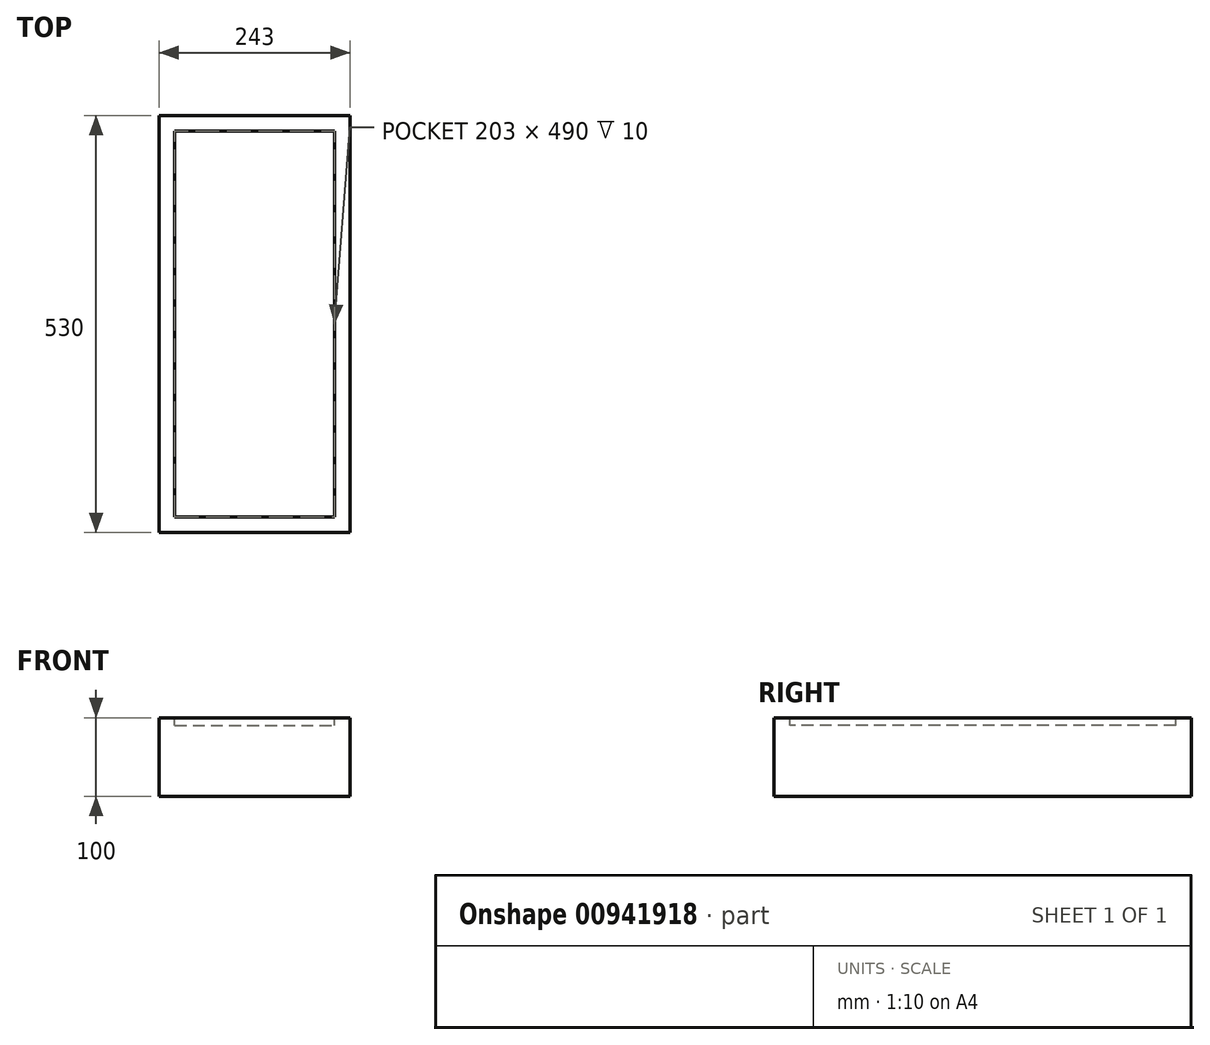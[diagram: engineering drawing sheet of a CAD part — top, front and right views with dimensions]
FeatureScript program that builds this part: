
annotation { "Feature Type Name" : "Feature", "Feature Type Description" : "" }
export const myFeature = defineFeature(function(context is Context, id is Id, definition is map)
    precondition{}
    {
        {
            var Q0;
            Q0=qCreatedBy(makeId("Top.planeOp"),FACE);
            var sketch = newSketch(context, id + "F0", { "sketchPlane" : qUnion([Q0])});
            skLineSegment(sketch, "E0.bottom", {"start": v(-266.27, 176.22) * mm, "end": v(-23.27, 176.22) * mm});
            skLineSegment(sketch, "E0.top", {"start": v(-266.27, -353.78) * mm, "end": v(-23.27, -353.78) * mm});
            skLineSegment(sketch, "E0.left", {"start": v(-266.27, 176.22) * mm, "end": v(-266.27, -353.78) * mm});
            skLineSegment(sketch, "E0.right", {"start": v(-23.27, 176.22) * mm, "end": v(-23.27, -353.78) * mm});
            skLineSegment(sketch, "E1.bottom", {"start": v(-246.27, 156.22) * mm, "end": v(-43.27, 156.22) * mm});
            skLineSegment(sketch, "E1.top", {"start": v(-246.27, -333.78) * mm, "end": v(-43.27, -333.78) * mm});
            skLineSegment(sketch, "E1.left", {"start": v(-246.27, 156.22) * mm, "end": v(-246.27, -333.78) * mm});
            skLineSegment(sketch, "E1.right", {"start": v(-43.27, 156.22) * mm, "end": v(-43.27, -333.78) * mm});
            skSolve(sketch);
        }
        {
            var Q0;
            Q0=makeQuery(id+"F0.imprint","IMPRINT",FACE,{"disambiguationData":[TD([[makeQuery(id+"F0.imprint","IMPRINT",EDGE,{"derivedFrom":sQuery(id+"F0.wireOp",EDGE,"E0.bottom")}),-1.0]])]});
            var Q1;
            Q1=makeQuery(id+"F0.imprint","IMPRINT",FACE,{"disambiguationData":[TD([[makeQuery(id+"F0.imprint","IMPRINT",EDGE,{"derivedFrom":sQuery(id+"F0.wireOp",EDGE,"E1.bottom")}),-1.0]])]});
            extrude(context, id + "F1", {"entities" : qUnion([Q0, Q1]), "oppositeDirection" : true, "depth" : 100 * mm, "offsetDistance" : 25 * mm});
        }
        {
            var Q0;
            Q0=makeQuery(id+"F0.imprint","IMPRINT",FACE,{"disambiguationData":[TD([[makeQuery(id+"F0.imprint","IMPRINT",EDGE,{"derivedFrom":sQuery(id+"F0.wireOp",EDGE,"E1.bottom")}),-1.0]])]});
            extrude(context, id + "F2", {"entities" : qUnion([Q0]), "operationType" : NewBodyOperationType.REMOVE, "oppositeDirection" : true, "depth" : 10 * mm, "offsetDistance" : 25 * mm});
        }
    });
